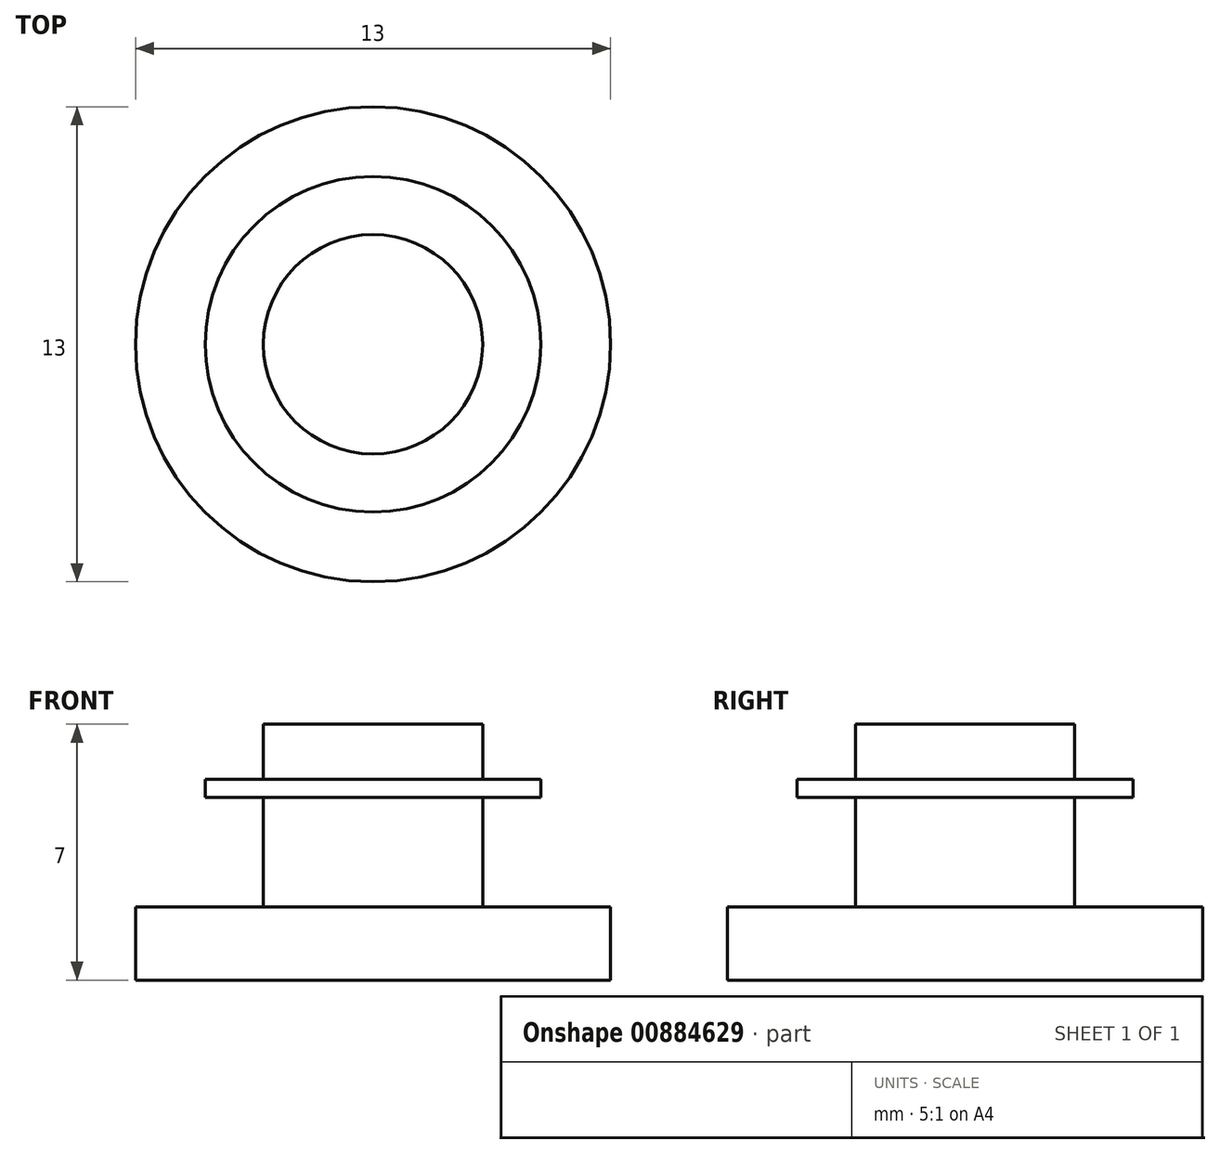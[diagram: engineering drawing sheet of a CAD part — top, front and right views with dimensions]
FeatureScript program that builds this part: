
annotation { "Feature Type Name" : "Feature", "Feature Type Description" : "" }
export const myFeature = defineFeature(function(context is Context, id is Id, definition is map)
    precondition{}
    {
        {
            var Q0;
            Q0=qCreatedBy(makeId("Top.planeOp"),FACE);
            var sketch = newSketch(context, id + "F0", { "sketchPlane" : qUnion([Q0])});
            skCircle(sketch, "E0", {"center": v(0, 0) * mm, "radius": 6.5 * mm});
            skSolve(sketch);
        }
        {
            var Q0;
            Q0=qSketchRegion(id+"F0",true);
            extrude(context, id + "F1", {"entities" : qUnion([Q0]), "depth" : 2 * mm, "offsetDistance" : 25 * mm});
        }
        {
            var Q0;
            Q0=makeQuery(id+"F1.opExtrude","CAP_FACE",FACE,{"disambiguationData":[OSD([sQuery(id+"F0.wireOp",EDGE,"E0")])],"isStart":false});
            var sketch = newSketch(context, id + "F2", { "sketchPlane" : qUnion([Q0])});
            skCircle(sketch, "E1", {"center": v(0, 0) * mm, "radius": 3 * mm});
            skSolve(sketch);
        }
        {
            var Q0;
            Q0=qSketchRegion(id+"F2",true);
            extrude(context, id + "F3", {"entities" : qUnion([Q0]), "operationType" : NewBodyOperationType.ADD, "depth" : 5 * mm, "offsetDistance" : 25 * mm});
        }
        {
            var Q0;
            Q0=qCreatedBy(makeId("Top.planeOp"),FACE);
            cPlane(context, id + "F4", {"entities" : qUnion([Q0]), "cplaneType" : CPlaneType.OFFSET, "offset" : 5 * mm, "width" : 150 * mm, "height" : 150 * mm});
        }
        {
            var Q0;
            Q0=qCreatedBy(id+"F4.planeOp",FACE);
            var sketch = newSketch(context, id + "F5", { "sketchPlane" : qUnion([Q0])});
            skCircle(sketch, "E2", {"center": v(0, 0) * mm, "radius": 4.6 * mm});
            skSolve(sketch);
        }
        {
            var Q0;
            Q0=qSketchRegion(id+"F5",true);
            extrude(context, id + "F6", {"entities" : qUnion([Q0]), "operationType" : NewBodyOperationType.ADD, "depth" : .5 * mm, "offsetDistance" : 25 * mm});
        }
    });
